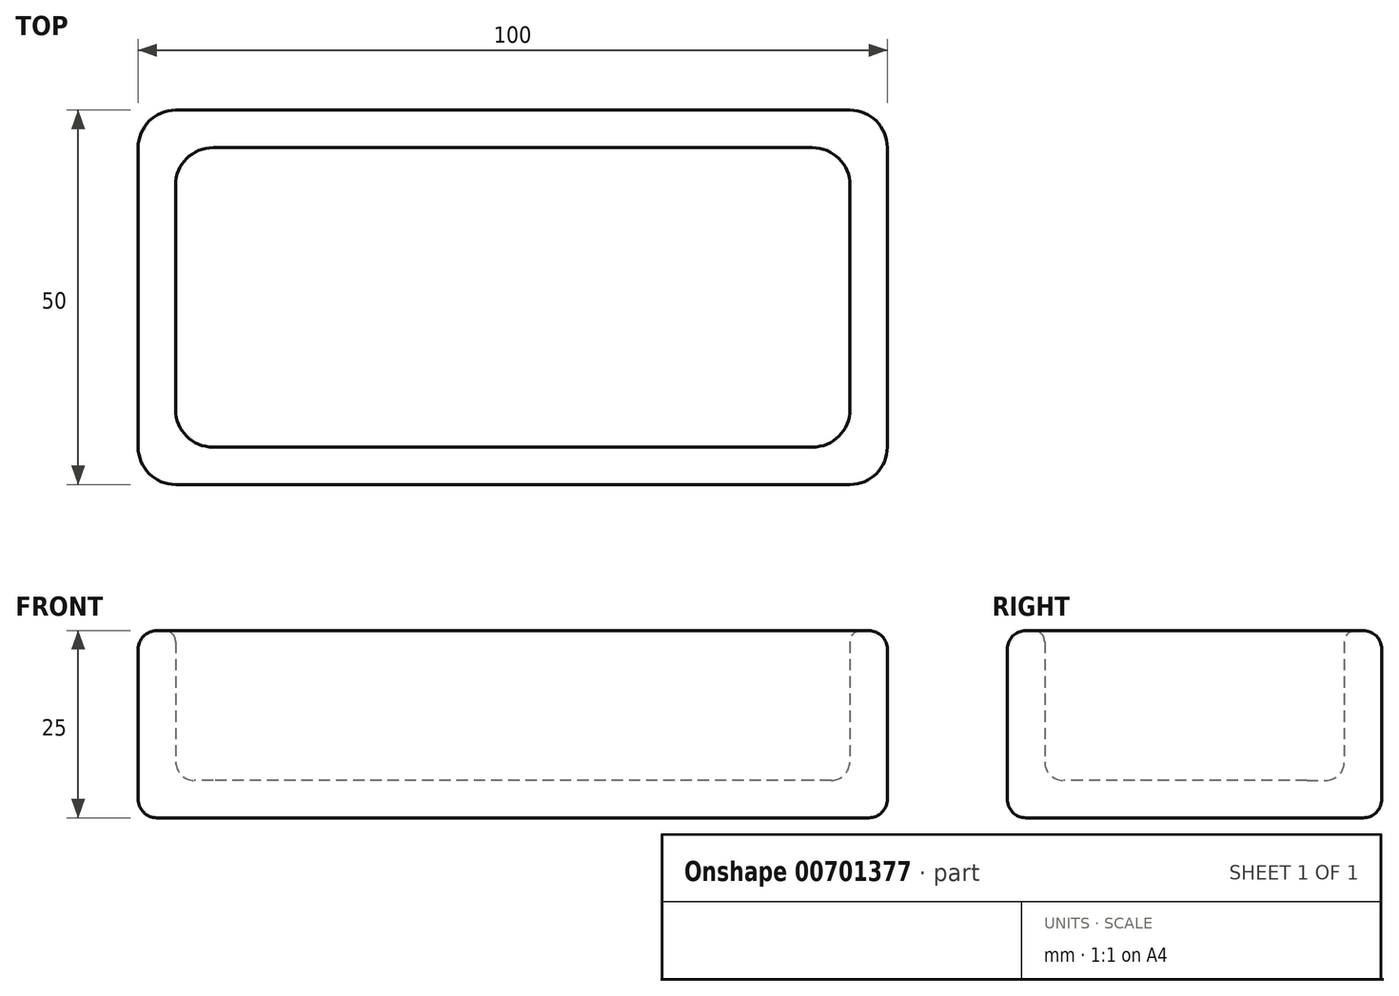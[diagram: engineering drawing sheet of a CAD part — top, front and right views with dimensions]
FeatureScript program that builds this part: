
annotation { "Feature Type Name" : "Feature", "Feature Type Description" : "" }
export const myFeature = defineFeature(function(context is Context, id is Id, definition is map)
    precondition{}
    {
        {
            var Q0;
            Q0=qCreatedBy(makeId("Top.planeOp"),FACE);
            var sketch = newSketch(context, id + "F0", { "sketchPlane" : qUnion([Q0])});
            skLineSegment(sketch, "E0.bottom", {"start": v(-50, 25) * mm, "end": v(50, 25) * mm});
            skLineSegment(sketch, "E0.top", {"start": v(-50, -25) * mm, "end": v(50, -25) * mm});
            skLineSegment(sketch, "E0.left", {"start": v(-50, 25) * mm, "end": v(-50, -25) * mm});
            skLineSegment(sketch, "E0.right", {"start": v(50, 25) * mm, "end": v(50, -25) * mm});
            skSolve(sketch);
        }
        {
            var Q0;
            Q0=makeQuery(id+"F0.imprint","IMPRINT",FACE,{"disambiguationData":[TD([[makeQuery(id+"F0.imprint","IMPRINT",EDGE,{"derivedFrom":sQuery(id+"F0.wireOp",EDGE,"E0.bottom")}),-1.0]])]});
            extrude(context, id + "F1", {"entities" : qUnion([Q0]), "depth" : 25 * mm, "offsetDistance" : 25 * mm});
        }
        {
            var Q0;
            Q0=makeQuery(id+"F1.opExtrude","SWEPT_EDGE",EDGE,{"disambiguationData":[OSD([sQuery(id+"F0.wireOp",EDGE,"E0.top"),sQuery(id+"F0.wireOp",EDGE,"E0.right")])]});
            var Q1;
            Q1=makeQuery(id+"F1.opExtrude","SWEPT_EDGE",EDGE,{"disambiguationData":[OSD([sQuery(id+"F0.wireOp",EDGE,"E0.bottom"),sQuery(id+"F0.wireOp",EDGE,"E0.right")])]});
            var Q2;
            Q2=makeQuery(id+"F1.opExtrude","SWEPT_EDGE",EDGE,{"disambiguationData":[OSD([sQuery(id+"F0.wireOp",EDGE,"E0.top"),sQuery(id+"F0.wireOp",EDGE,"E0.left")])]});
            var Q3;
            Q3=makeQuery(id+"F1.opExtrude","SWEPT_EDGE",EDGE,{"disambiguationData":[OSD([sQuery(id+"F0.wireOp",EDGE,"E0.bottom"),sQuery(id+"F0.wireOp",EDGE,"E0.left")])]});
            fillet(context, id + "F2", {"entities" : qUnion([Q0, Q1, Q2, Q3]), "radius" : 5 * mm, "tangentPropagation" : true, "allowEdgeOverflow" : false});
        }
        {
            var Q0;
            Q0=makeQuery(id+"F1.opExtrude","CAP_EDGE",EDGE,{"disambiguationData":[OSD([sQuery(id+"F0.wireOp",EDGE,"E0.right")])],"isStart":false});
            var Q1;
            Q1=makeQuery(id+"F1.opExtrude","CAP_EDGE",EDGE,{"disambiguationData":[OSD([sQuery(id+"F0.wireOp",EDGE,"E0.right")])],"isStart":true});
            fillet(context, id + "F3", {"entities" : qUnion([Q0, Q1]), "radius" : 2.5 * mm, "tangentPropagation" : true, "allowEdgeOverflow" : false});
        }
        {
            var Q0;
            Q0=makeQuery(id+"F1.opExtrude","SWEPT_BODY",BODY,{"disambiguationData":[OSD([sQuery(id+"F0.wireOp",EDGE,"E0.bottom"),sQuery(id+"F0.wireOp",EDGE,"E0.top"),sQuery(id+"F0.wireOp",EDGE,"E0.left"),sQuery(id+"F0.wireOp",EDGE,"E0.right")])]});
            var Q1;
            Q1=qCreatedBy(makeId("Front.planeOp"),FACE);
            mirror(context, id + "F4", {"operationType" : NewBodyOperationType.INTERSECT, "entities" : qUnion([Q0]), "mirrorPlane" : qUnion([Q1])});
        }
        {
            var Q0;
            Q0=makeQuery(id+"F1.opExtrude","CAP_FACE",FACE,{"disambiguationData":[OSD([sQuery(id+"F0.wireOp",EDGE,"E0.bottom"),sQuery(id+"F0.wireOp",EDGE,"E0.top"),sQuery(id+"F0.wireOp",EDGE,"E0.left"),sQuery(id+"F0.wireOp",EDGE,"E0.right")])],"isStart":false});
            shell(context, id + "F5", {"entities" : qUnion([Q0]), "thickness" : 5 * mm});
        }
        {
            var Q0;
            Q0=makeQuery(id+"F5.opShell","OFFSET_EDGE",EDGE,{"disambiguationData":[OSD([sQuery(id+"F0.wireOp",EDGE,"E0.bottom"),sQuery(id+"F0.wireOp",EDGE,"E0.left")])]});
            var Q1;
            Q1=makeQuery(id+"F5.opShell","OFFSET_EDGE",EDGE,{"disambiguationData":[OSD([sQuery(id+"F0.wireOp",EDGE,"E0.bottom"),sQuery(id+"F0.wireOp",EDGE,"E0.right")])]});
            var Q2;
            Q2=makeQuery(id+"F5.opShell","OFFSET_EDGE",EDGE,{"disambiguationData":[OSD([sQuery(id+"F0.wireOp",EDGE,"E0.top"),sQuery(id+"F0.wireOp",EDGE,"E0.left")])]});
            var Q3;
            Q3=makeQuery(id+"F5.opShell","OFFSET_EDGE",EDGE,{"disambiguationData":[OSD([sQuery(id+"F0.wireOp",EDGE,"E0.top"),sQuery(id+"F0.wireOp",EDGE,"E0.right")])]});
            fillet(context, id + "F6", {"entities" : qUnion([Q0, Q1, Q2, Q3]), "radius" : 5 * mm, "tangentPropagation" : true, "allowEdgeOverflow" : false});
        }
        {
            var Q0;
            {var subQ0=sQuery(id+"F0.wireOp",EDGE,"E0.right");Q0=makeQuery(id+"F3.opFillet","BLEND_EDGE",EDGE,{"blendedFrom":[makeQuery(id+"F1.opExtrude","CAP_EDGE",EDGE,{"disambiguationData":[OSD([subQ0])],"isStart":false}),makeQuery(id+"F1.opExtrude","SWEPT_FACE",FACE,{"disambiguationData":[OSD([subQ0])]})],"blendedInto":[makeQuery(id+"F1.opExtrude","SWEPT_FACE",FACE,{"disambiguationData":[OSD([subQ0])]})]});}
            var Q1;
            {var subQ0=sQuery(id+"F0.wireOp",EDGE,"E0.right");var subQ1=sQuery(id+"F0.wireOp",EDGE,"E0.left");var subQ2=sQuery(id+"F0.wireOp",EDGE,"E0.top");var subQ3=sQuery(id+"F0.wireOp",EDGE,"E0.bottom");var subQ4=makeQuery(id+"F1.opExtrude","CAP_EDGE",EDGE,{"disambiguationData":[OSD([subQ3])],"isStart":true});Q1=makeQuery(id+"F5.opShell","OFFSET_EDGE",EDGE,{"disambiguationData":[OSD([subQ3,subQ2,subQ1,subQ0]),TDD([makeQuery(id+"F3.opFillet","BLEND_EDGE",EDGE,{"blendedFrom":[subQ4,makeQuery(id+"F1.opExtrude","SWEPT_FACE",FACE,{"disambiguationData":[OSD([subQ3])]})],"blendedInto":[makeQuery(id+"F1.opExtrude","SWEPT_FACE",FACE,{"disambiguationData":[OSD([subQ3])]})]}),makeQuery(id+"F3.opFillet","BLEND_EDGE",EDGE,{"blendedFrom":[subQ4,makeQuery(id+"F1.opExtrude","CAP_FACE",FACE,{"disambiguationData":[OSD([subQ3,subQ2,subQ1,subQ0])],"isStart":true})],"blendedInto":[makeQuery(id+"F1.opExtrude","CAP_FACE",FACE,{"disambiguationData":[OSD([subQ3,subQ2,subQ1,subQ0])],"isStart":true})]})])]});}
            fillet(context, id + "F7", {"entities" : qUnion([Q0, Q1]), "radius" : 2.5 * mm, "tangentPropagation" : true, "allowEdgeOverflow" : false});
        }
        {
            var Q0;
            {var subQ0=sQuery(id+"F0.wireOp",EDGE,"E0.right");var subQ1=sQuery(id+"F0.wireOp",EDGE,"E0.left");var subQ2=sQuery(id+"F0.wireOp",EDGE,"E0.top");var subQ3=sQuery(id+"F0.wireOp",EDGE,"E0.bottom");var subQ4=makeQuery(id+"F1.opExtrude","CAP_EDGE",EDGE,{"disambiguationData":[OSD([subQ3])],"isStart":false});Q0=makeQuery(id+"F5.opShell","OFFSET_EDGE",EDGE,{"disambiguationData":[OSD([subQ3,subQ2,subQ1,subQ0]),TDD([makeQuery(id+"F3.opFillet","BLEND_EDGE",EDGE,{"blendedFrom":[subQ4,makeQuery(id+"F1.opExtrude","SWEPT_FACE",FACE,{"disambiguationData":[OSD([subQ3])]})],"blendedInto":[makeQuery(id+"F1.opExtrude","SWEPT_FACE",FACE,{"disambiguationData":[OSD([subQ3])]})]}),makeQuery(id+"F3.opFillet","BLEND_EDGE",EDGE,{"blendedFrom":[subQ4,makeQuery(id+"F1.opExtrude","CAP_FACE",FACE,{"disambiguationData":[OSD([subQ3,subQ2,subQ1,subQ0])],"isStart":false})],"blendedInto":[makeQuery(id+"F1.opExtrude","CAP_FACE",FACE,{"disambiguationData":[OSD([subQ3,subQ2,subQ1,subQ0])],"isStart":false})]})])]});}
            fillet(context, id + "F8", {"entities" : qUnion([Q0]), "radius" : 1.5 * mm, "tangentPropagation" : true, "allowEdgeOverflow" : false});
        }
    });
